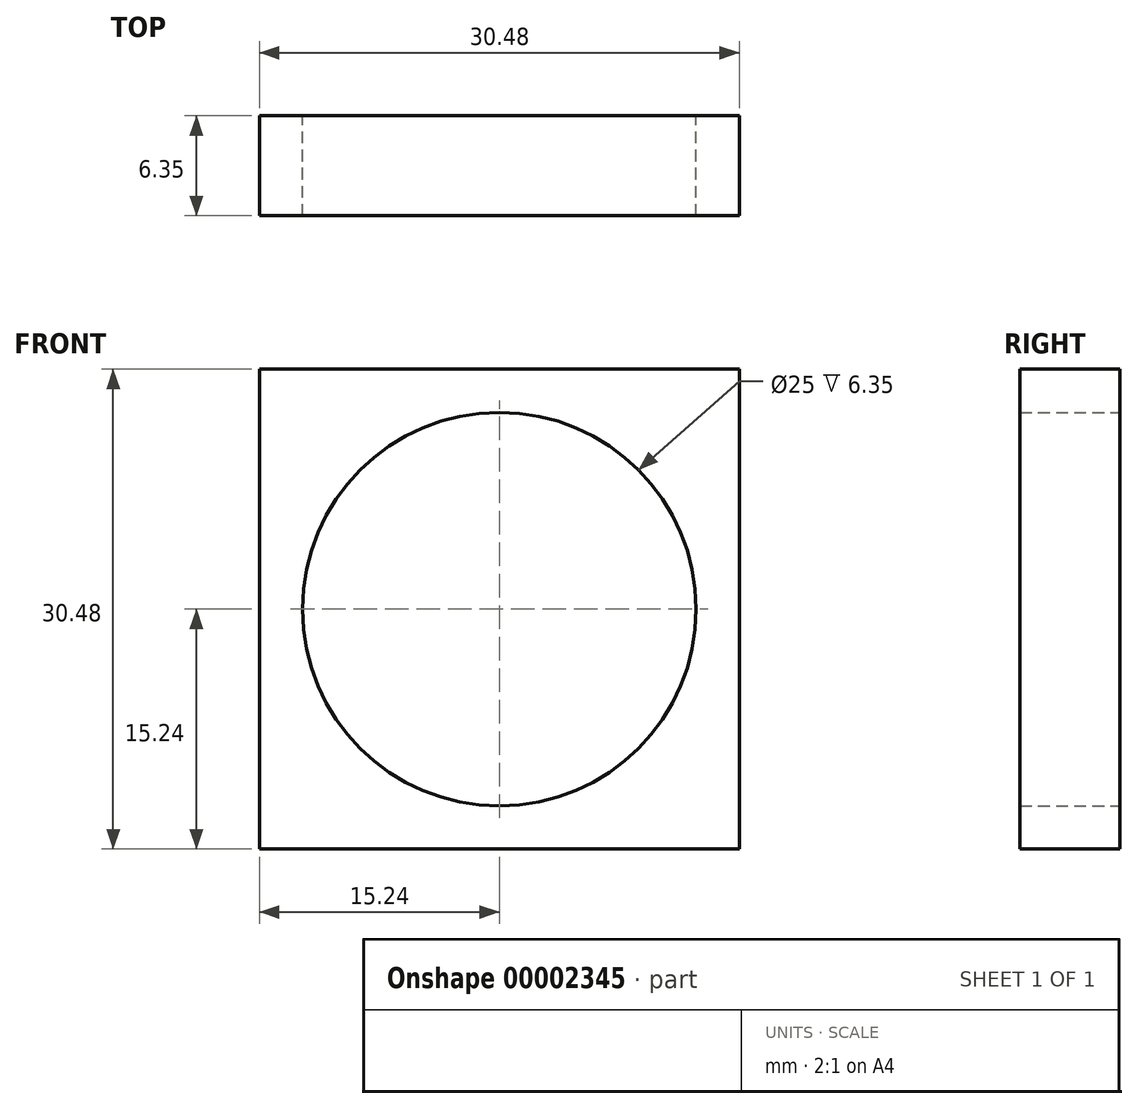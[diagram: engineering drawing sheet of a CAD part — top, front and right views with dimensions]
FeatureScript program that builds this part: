
annotation { "Feature Type Name" : "Feature", "Feature Type Description" : "" }
export const myFeature = defineFeature(function(context is Context, id is Id, definition is map)
    precondition{}
    {
        {
            var Q0;
            Q0=qCreatedBy(makeId("Front.planeOp"),FACE);
            var sketch = newSketch(context, id + "F0", { "sketchPlane" : qUnion([Q0])});
            skLineSegment(sketch, "E0.rect.bottom", {"start": v(0, 7.85) * mm, "end": v(0, 7.85) * mm});
            skLineSegment(sketch, "E0.rect.top", {"start": v(0, -7.85) * mm, "end": v(0, -7.85) * mm});
            skLineSegment(sketch, "E1.0.MirrorCS", {"start": v(-5.96, 7.85) * mm, "end": v(-5.96, 7.85) * mm});
            skCircle(sketch, "E2", {"center": v(0, 0) * mm, "radius": 12.5 * mm});
            skLineSegment(sketch, "E3.rect.bottom", {"start": v(15.24, 15.24) * mm, "end": v(-15.24, 15.24) * mm});
            skLineSegment(sketch, "E3.rect.top", {"start": v(15.24, -15.24) * mm, "end": v(-15.24, -15.24) * mm});
            skLineSegment(sketch, "E3.rect.left", {"start": v(15.24, 15.24) * mm, "end": v(15.24, -15.24) * mm});
            skLineSegment(sketch, "E3.rect.right", {"start": v(-15.24, 15.24) * mm, "end": v(-15.24, -15.24) * mm});
            skSolve(sketch);
        }
        {
            var Q0;
            Q0 = qSketchRegion(id + "F0", true);
            extrude(context, id + "F1", {"entities" : qUnion([Q0]), "depth" : 6.35 * mm});
        }
    });
